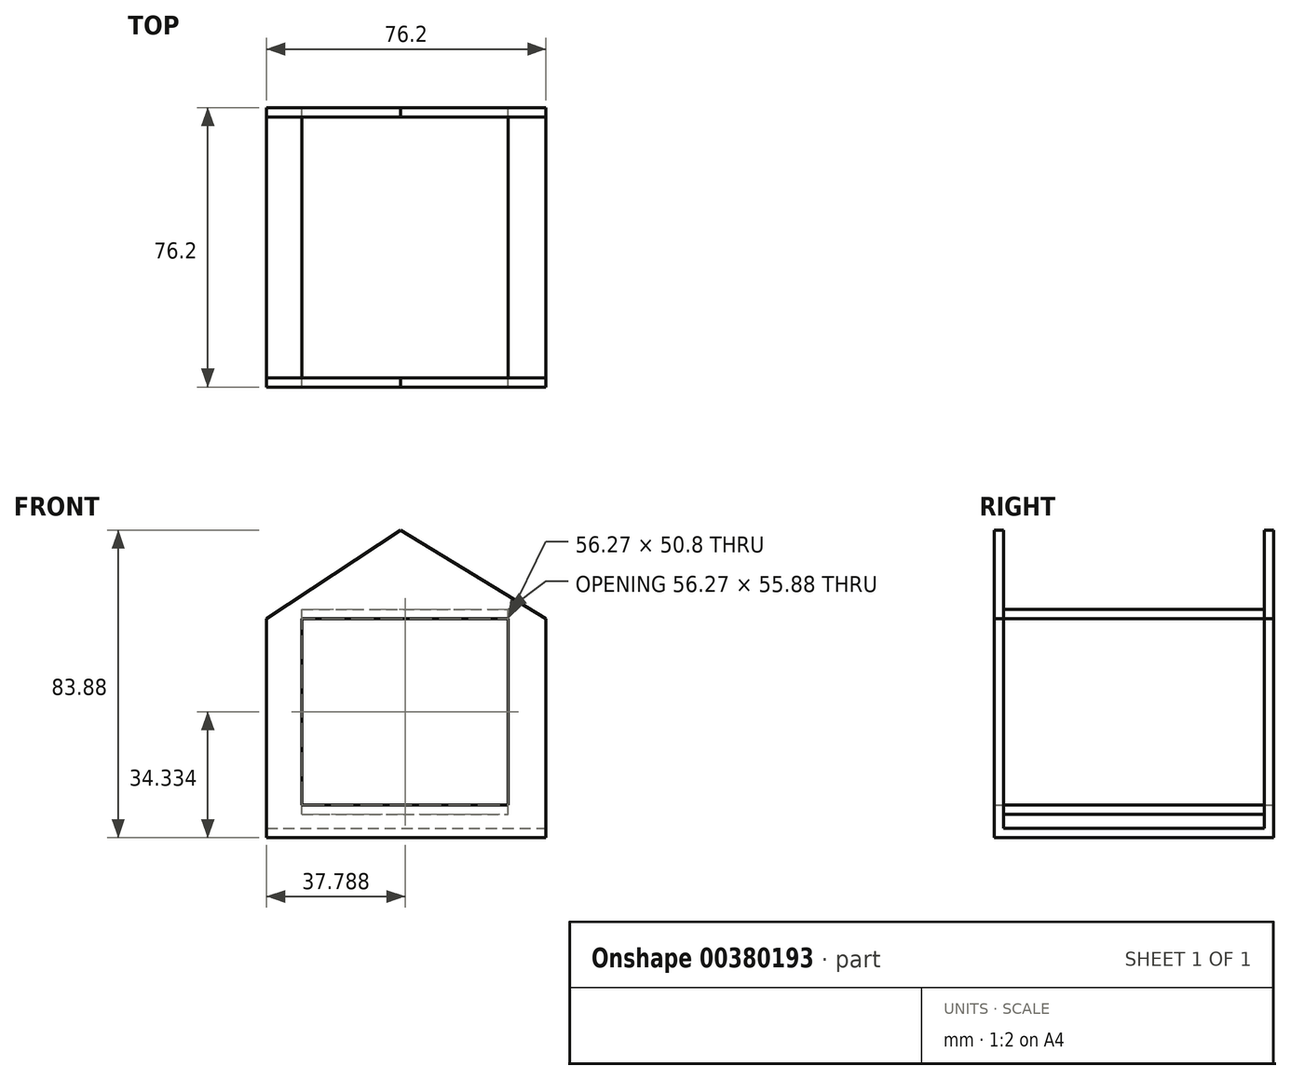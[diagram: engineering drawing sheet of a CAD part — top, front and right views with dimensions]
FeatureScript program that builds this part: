
annotation { "Feature Type Name" : "Feature", "Feature Type Description" : "" }
export const myFeature = defineFeature(function(context is Context, id is Id, definition is map)
    precondition{}
    {
        {
            var Q0;
            Q0=qCreatedBy(makeId("Front.planeOp"),FACE);
            var sketch = newSketch(context, id + "F0", { "sketchPlane" : qUnion([Q0])});
            skLineSegment(sketch, "E0", {"start": v(-41.43, 26.15) * mm, "end": v(-41.43, -24.65) * mm});
            skLineSegment(sketch, "E1", {"start": v(-41.43, -24.65) * mm, "end": v(-31.78, -24.65) * mm});
            skLineSegment(sketch, "E2", {"start": v(-31.78, -24.65) * mm, "end": v(-31.78, 26.15) * mm});
            skLineSegment(sketch, "E3", {"start": v(-31.78, 26.15) * mm, "end": v(-41.43, 26.15) * mm});
            skLineSegment(sketch, "E4", {"start": v(-41.43, 26.15) * mm, "end": v(-4.9, 50.3) * mm});
            skLineSegment(sketch, "E5", {"start": v(-4.9, 50.3) * mm, "end": v(34.77, 26.15) * mm});
            skLineSegment(sketch, "E6", {"start": v(34.77, 26.15) * mm, "end": v(34.77, -24.65) * mm});
            skLineSegment(sketch, "E7", {"start": v(34.77, -24.65) * mm, "end": v(24.5, -24.65) * mm});
            skLineSegment(sketch, "E8", {"start": v(24.5, -24.65) * mm, "end": v(24.5, 26.15) * mm});
            skLineSegment(sketch, "E9", {"start": v(24.5, 26.15) * mm, "end": v(34.77, 26.15) * mm});
            skLineSegment(sketch, "E10", {"start": v(-41.43, -24.65) * mm, "end": v(-41.43, -33.58) * mm});
            skLineSegment(sketch, "E11", {"start": v(-41.43, -24.65) * mm, "end": v(34.77, -24.65) * mm});
            skLineSegment(sketch, "E12", {"start": v(-41.43, -33.58) * mm, "end": v(34.77, -33.58) * mm});
            skLineSegment(sketch, "E13", {"start": v(34.77, -24.65) * mm, "end": v(34.77, -33.58) * mm});
            skLineSegment(sketch, "E14", {"start": v(-41.43, 26.15) * mm, "end": v(34.77, 26.15) * mm});
            skSolve(sketch);
        }
        {
            var Q0;
            {var subQ3=sQuery(id+"F0.wireOp",EDGE,"E4");Q0=makeQuery(id+"F0.imprint","IMPRINT",FACE,{"disambiguationData":[TD([[makeQuery(id+"F0.imprint","IMPRINT",EDGE,{"derivedFrom":subQ3}),-1.0]])]});}
            var Q1;
            {var subQ0=sQuery(id+"F0.wireOp",EDGE,"E6");Q1=makeQuery(id+"F0.imprint","IMPRINT",FACE,{"disambiguationData":[TD([[makeQuery(id+"F0.imprint","IMPRINT",EDGE,{"derivedFrom":subQ0}),-1.0]])]});}
            var Q2;
            {var subQ0=sQuery(id+"F0.wireOp",EDGE,"E0");Q2=makeQuery(id+"F0.imprint","IMPRINT",FACE,{"disambiguationData":[TD([[makeQuery(id+"F0.imprint","IMPRINT",EDGE,{"derivedFrom":subQ0}),1.0]])]});}
            var Q3;
            {var subQ4=sQuery(id+"F0.wireOp",EDGE,"E10");Q3=makeQuery(id+"F0.imprint","IMPRINT",FACE,{"disambiguationData":[TD([[makeQuery(id+"F0.imprint","IMPRINT",EDGE,{"derivedFrom":subQ4}),1.0]])]});}
            extrude(context, id + "F1", {"entities" : qUnion([Q0, Q1, Q2, Q3]), "depth" : 76.2 * mm});
        }
        {
            var Q0;
            Q0=makeQuery(id+"F1.opExtrude","SWEPT_FACE",FACE,{"disambiguationData":[OSD([sQuery(id+"F0.wireOp",EDGE,"E6"),sQuery(id+"F0.wireOp",EDGE,"E13")])]});
            var Q1;
            Q1=makeQuery(id+"F1.opExtrude","SWEPT_FACE",FACE,{"disambiguationData":[OSD([sQuery(id+"F0.wireOp",EDGE,"E8")])]});
            var Q2;
            Q2=makeQuery(id+"F1.opExtrude","SWEPT_FACE",FACE,{"disambiguationData":[OSD([sQuery(id+"F0.wireOp",EDGE,"E0"),sQuery(id+"F0.wireOp",EDGE,"E10")])]});
            var Q3;
            Q3=makeQuery(id+"F1.opExtrude","SWEPT_FACE",FACE,{"disambiguationData":[OSD([sQuery(id+"F0.wireOp",EDGE,"E2")])]});
            var Q4;
            Q4=makeQuery(id+"F1.opExtrude","SWEPT_FACE",FACE,{"disambiguationData":[OSD([sQuery(id+"F0.wireOp",EDGE,"E4")])]});
            var Q5;
            Q5=makeQuery(id+"F1.opExtrude","SWEPT_FACE",FACE,{"disambiguationData":[OSD([sQuery(id+"F0.wireOp",EDGE,"E5")])]});
            shell(context, id + "F2", {"entities" : qUnion([Q0, Q1, Q2, Q3, Q4, Q5]), "thickness" : 2.54 * mm});
        }
    });
